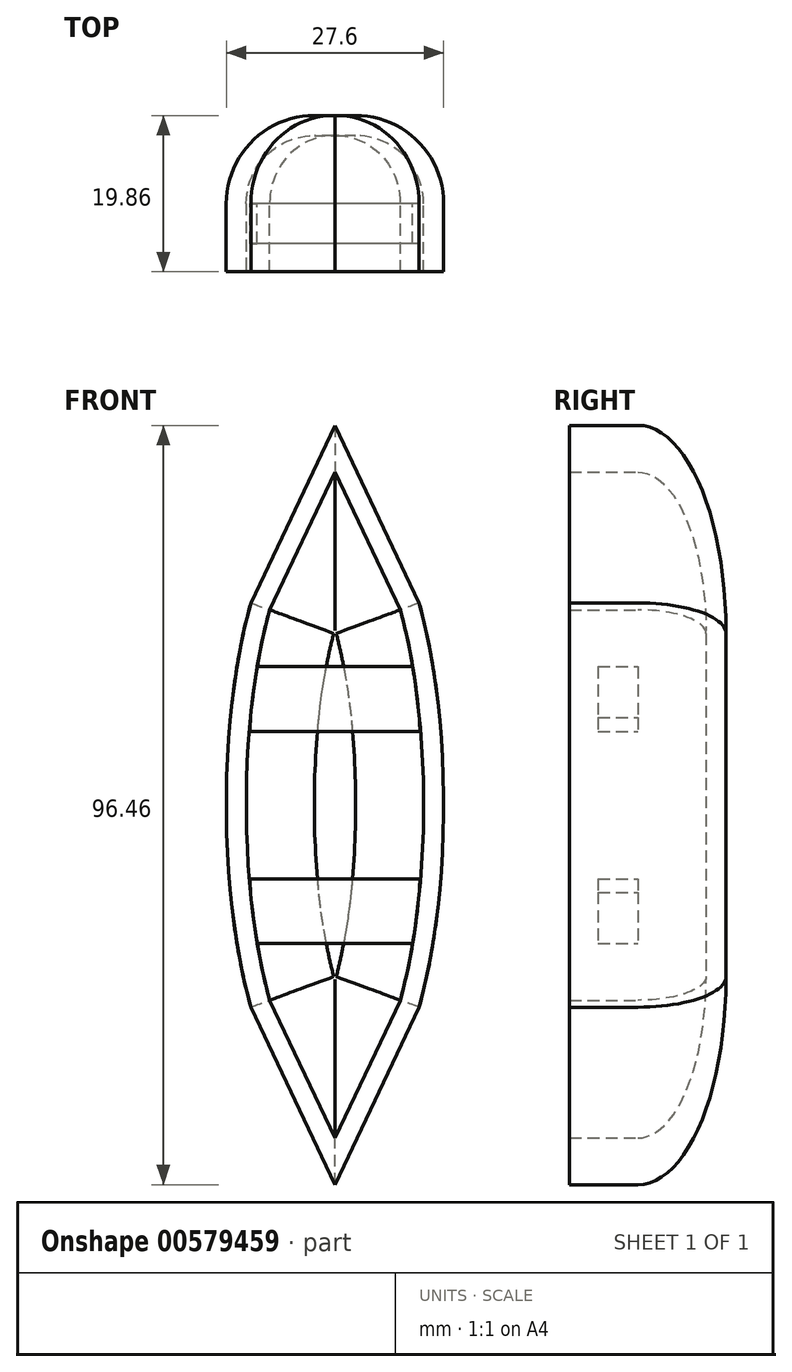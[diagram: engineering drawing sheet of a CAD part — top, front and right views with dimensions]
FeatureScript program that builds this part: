
annotation { "Feature Type Name" : "Feature", "Feature Type Description" : "" }
export const myFeature = defineFeature(function(context is Context, id is Id, definition is map)
    precondition{}
    {
        {
            var Q0;
            Q0=qCreatedBy(makeId("Front.planeOp"),FACE);
            var sketch = newSketch(context, id + "F0", { "sketchPlane" : qUnion([Q0])});
            skLineSegment(sketch, "E0", {"start": v(-10.69, 25.68) * mm, "end": v(0, 48.23) * mm});
            skPoint(sketch, "E0.endSnap0", {"position": v(0, 40.57) * mm});
            skLineSegment(sketch, "E1", {"start": v(0, 48.23) * mm, "end": v(10.69, 25.68) * mm});
            skEllipticalArc(sketch, "E2.trimOffspring", {});
            skLineSegment(sketch, "E3.MirrorCS", {"start": v(0, -48.23) * mm, "end": v(10.69, -25.68) * mm});
            skLineSegment(sketch, "E4.MirrorCS", {"start": v(-10.69, -25.68) * mm, "end": v(0, -48.23) * mm});
            skEllipticalArc(sketch, "E5.trimOffspring", {});
            const initialGuessF0  = {"E2.trimOffspring": [0, 0, 0, 1, 0.04057244583964348, 0.013804851844751836, 0.8854303472803569, 2.2561623063094363], "E5.trimOffspring": [0, 0, 0, 1, 0.04057244583964348, 0.013804851844751836, 4.02702300087015, 5.397754959899229]};
            skSetInitialGuess(sketch, initialGuessF0);
            skSolve(sketch);
        }
        {
            var Q0;
            Q0=makeQuery(id+"F0.imprint","IMPRINT",FACE,{"disambiguationData":[TD([[makeQuery(id+"F0.imprint","IMPRINT",EDGE,{"derivedFrom":sQuery(id+"F0.wireOp",EDGE,"E0")}),-1.0]])]});
            extrude(context, id + "F1", {"entities" : qUnion([Q0]), "depth" : 25.4 * mm, "offsetDistance" : 25.4 * mm});
        }
        {
            var Q0;
            Q0=makeQuery(id+"F1.opExtrude","CAP_FACE",FACE,{"disambiguationData":[OSD([sQuery(id+"F0.wireOp",EDGE,"E0"),sQuery(id+"F0.wireOp",EDGE,"E1"),sQuery(id+"F0.wireOp",EDGE,"E2.trimOffspring"),sQuery(id+"F0.wireOp",EDGE,"E3.MirrorCS"),sQuery(id+"F0.wireOp",EDGE,"E4.MirrorCS"),sQuery(id+"F0.wireOp",EDGE,"E5.trimOffspring")])],"isStart":true});
            fillet(context, id + "F2", {"entities" : qUnion([Q0]), "radius" : 11.18 * mm, "tangentPropagation" : true, "allowEdgeOverflow" : false});
        }
        {
            var Q0;
            Q0=qCreatedBy(makeId("Right.planeOp"),FACE);
            var sketch = newSketch(context, id + "F3", { "sketchPlane" : qUnion([Q0])});
            skLineSegment(sketch, "E6", {"start": v(-19.86, 48.23) * mm, "end": v(-19.86, -48.8) * mm});
            skLineSegment(sketch, "E7", {"start": v(-19.86, -48.8) * mm, "end": v(-34.05, -48.8) * mm});
            skLineSegment(sketch, "E8", {"start": v(-34.05, -48.8) * mm, "end": v(-34.05, 52.77) * mm});
            skLineSegment(sketch, "E9", {"start": v(-34.05, 52.77) * mm, "end": v(-19.86, 52.77) * mm});
            skLineSegment(sketch, "E10", {"start": v(-19.86, 52.77) * mm, "end": v(-19.86, 48.23) * mm});
            skSolve(sketch);
        }
        {
            var Q0;
            Q0=makeQuery(id+"F3.imprint","IMPRINT",FACE,{"disambiguationData":[TD([[makeQuery(id+"F3.imprint","IMPRINT",EDGE,{"derivedFrom":sQuery(id+"F3.wireOp",EDGE,"E6")}),-1.0]])]});
            extrude(context, id + "F4", {"entities" : qUnion([Q0]), "operationType" : NewBodyOperationType.REMOVE, "endBound" : BoundingType.THROUGH_ALL, "oppositeDirection" : true, "depth" : 25.4 * mm, "offsetDistance" : 25.4 * mm});
        }
        {
            var Q0;
            Q0=qCreatedBy(makeId("Right.planeOp"),FACE);
            var sketch = newSketch(context, id + "F5", { "sketchPlane" : qUnion([Q0])});
            skLineSegment(sketch, "E11", {"start": v(-19.86, 48.23) * mm, "end": v(-19.86, 56.74) * mm});
            skLineSegment(sketch, "E12", {"start": v(-19.86, 56.74) * mm, "end": v(-37.45, 56.74) * mm});
            skLineSegment(sketch, "E13", {"start": v(-37.45, 56.74) * mm, "end": v(-37.45, -60.43) * mm});
            skLineSegment(sketch, "E14", {"start": v(-19.86, -48.23) * mm, "end": v(-19.86, -60.43) * mm});
            skLineSegment(sketch, "E15", {"start": v(-19.86, -60.43) * mm, "end": v(-37.45, -60.43) * mm});
            skLineSegment(sketch, "E16", {"start": v(-19.86, 48.23) * mm, "end": v(-19.86, -48.23) * mm});
            skSolve(sketch);
        }
        {
            var Q0;
            Q0 = qSketchRegion(id + "F5", true);
            extrude(context, id + "F6", {"entities" : qUnion([Q0]), "operationType" : NewBodyOperationType.REMOVE, "endBound" : BoundingType.THROUGH_ALL, "depth" : 25.4 * mm, "offsetDistance" : 25.4 * mm});
        }
        {
            var Q0;
            Q0=makeQuery(id+"F6.boolean.opBoolean","MERGE",FACE,{"derivedFrom":[makeQuery(id+"F4.boolean.opBoolean","COPY",FACE,{"derivedFrom":makeQuery(id+"F4.opExtrude","SWEPT_FACE",FACE,{"disambiguationData":[OSD([sQuery(id+"F3.wireOp",EDGE,"E6"),sQuery(id+"F3.wireOp",EDGE,"E10")])]})}),makeQuery(id+"F6.opExtrude","SWEPT_FACE",FACE,{"disambiguationData":[OSD([sQuery(id+"F5.wireOp",EDGE,"E11"),sQuery(id+"F5.wireOp",EDGE,"E14"),sQuery(id+"F5.wireOp",EDGE,"E16")])]})]});
            shell(context, id + "F7", {"entities" : qUnion([Q0]), "thickness" : 2.54 * mm});
        }
        {
            var Q0;
            Q0=qCreatedBy(makeId("Front.planeOp"),FACE);
            cPlane(context, id + "F8", {"entities" : qUnion([Q0]), "cplaneType" : CPlaneType.OFFSET, "offset" : 11.18 * mm, "width" : 152.4 * mm, "height" : 152.4 * mm});
        }
        {
            var Q0;
            Q0=qCreatedBy(id+"F8.planeOp",FACE);
            var sketch = newSketch(context, id + "F9", { "sketchPlane" : qUnion([Q0])});
            skLineSegment(sketch, "E17", {"start": v(0, 9.36) * mm, "end": v(-10.78, 9.36) * mm});
            skLineSegment(sketch, "E18", {"start": v(0, 17.6) * mm, "end": v(-9.93, 17.6) * mm});
            skArc(sketch, "E19", {"start": v(-9.93, 17.6) * mm, "mid": v(-10.54, 13.5) * mm, "end": v(-10.78, 9.36) * mm});
            skLineSegment(sketch, "E20.MirrorCS", {"start": v(0, 9.36) * mm, "end": v(10.78, 9.36) * mm});
            skArc(sketch, "E21.MirrorCS", {"start": v(9.93, 17.6) * mm, "mid": v(10.54, 13.5) * mm, "end": v(10.78, 9.36) * mm});
            skLineSegment(sketch, "E22.MirrorCS", {"start": v(0, 17.6) * mm, "end": v(9.93, 17.6) * mm});
            skLineSegment(sketch, "E23.MirrorCS", {"start": v(0, -9.36) * mm, "end": v(10.78, -9.36) * mm});
            skLineSegment(sketch, "E24.MirrorCS", {"start": v(0, -9.36) * mm, "end": v(-10.78, -9.36) * mm});
            skArc(sketch, "E25.MirrorCS", {"start": v(-9.93, -17.6) * mm, "mid": v(-10.54, -13.5) * mm, "end": v(-10.78, -9.36) * mm});
            skLineSegment(sketch, "E26.MirrorCS", {"start": v(0, -17.6) * mm, "end": v(-9.93, -17.6) * mm});
            skLineSegment(sketch, "E27.MirrorCS", {"start": v(0, -17.6) * mm, "end": v(9.93, -17.6) * mm});
            skArc(sketch, "E28.MirrorCS", {"start": v(9.93, -17.6) * mm, "mid": v(10.54, -13.5) * mm, "end": v(10.78, -9.36) * mm});
            skSolve(sketch);
        }
        {
            var Q0;
            Q0 = qSketchRegion(id + "F9", true);
            extrude(context, id + "F10", {"entities" : qUnion([Q0]), "operationType" : NewBodyOperationType.ADD, "depth" : 5.08 * mm, "offsetDistance" : 25.4 * mm});
        }
    });
